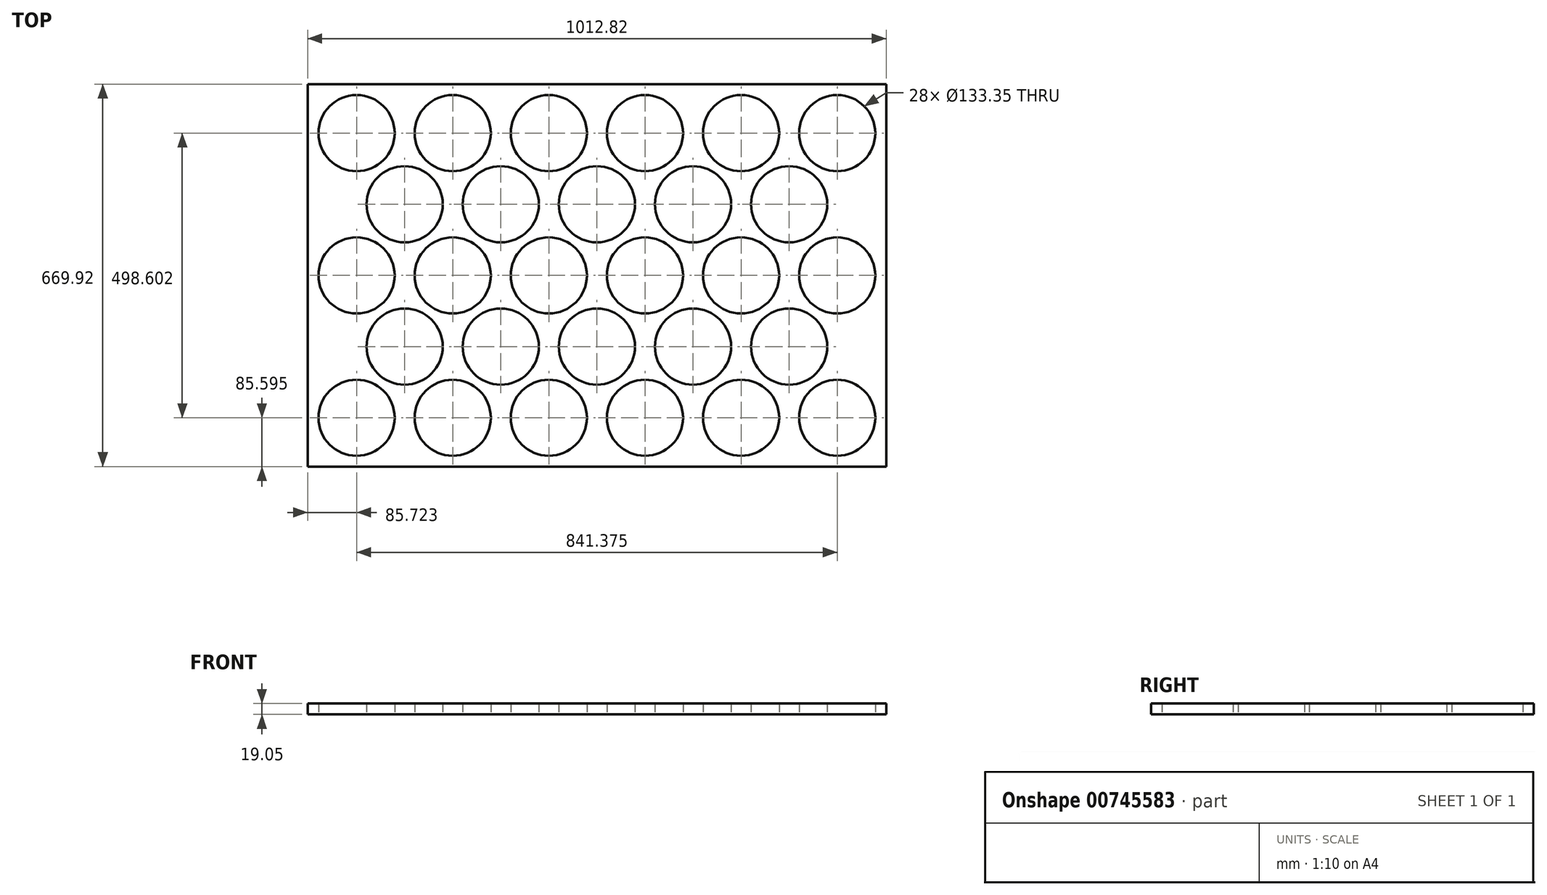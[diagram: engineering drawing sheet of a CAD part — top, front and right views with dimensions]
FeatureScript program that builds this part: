
annotation { "Feature Type Name" : "Feature", "Feature Type Description" : "" }
export const myFeature = defineFeature(function(context is Context, id is Id, definition is map)
    precondition{}
    {
        {
            var Q0;
            Q0=qCreatedBy(makeId("Top.planeOp"),FACE);
            var sketch = newSketch(context, id + "F0", { "sketchPlane" : qUnion([Q0])});
            skLineSegment(sketch, "E0.bottom", {"start": v(-506.41, 334.96) * mm, "end": v(506.41, 334.96) * mm});
            skLineSegment(sketch, "E0.top", {"start": v(-506.41, -334.96) * mm, "end": v(506.41, -334.96) * mm});
            skLineSegment(sketch, "E0.left", {"start": v(-506.41, 334.96) * mm, "end": v(-506.41, -334.96) * mm});
            skLineSegment(sketch, "E0.right", {"start": v(506.41, 334.96) * mm, "end": v(506.41, -334.96) * mm});
            skPoint(sketch, "E0.middle", {"position": v(0, 0) * mm});
            skCircle(sketch, "E1", {"center": v(-420.69, 249.24) * mm, "radius": 66.68 * mm});
            skLineSegment(sketch, "E2", {"start": v(-506.41, -334.96) * mm, "end": v(-506.41, -249.24) * mm, "construction": true});
            skLineSegment(sketch, "E3", {"start": v(-506.41, -249.24) * mm, "end": v(506.41, -249.24) * mm, "construction": true});
            skLineSegment(sketch, "E4", {"start": v(506.41, 334.96) * mm, "end": v(420.69, 334.96) * mm, "construction": true});
            skLineSegment(sketch, "E5", {"start": v(420.69, 334.96) * mm, "end": v(420.69, -249.24) * mm, "construction": true});
            skCircle(sketch, "E6.0.1.0", {"center": v(-420.69, -0.06) * mm, "radius": 66.68 * mm});
            skCircle(sketch, "E6.0.2.0", {"center": v(-420.69, -249.36) * mm, "radius": 66.68 * mm});
            skCircle(sketch, "E6.1.0.0", {"center": v(-252.41, 249.24) * mm, "radius": 66.68 * mm});
            skCircle(sketch, "E6.1.1.0", {"center": v(-252.41, -0.06) * mm, "radius": 66.68 * mm});
            skCircle(sketch, "E6.1.2.0", {"center": v(-252.41, -249.36) * mm, "radius": 66.68 * mm});
            skCircle(sketch, "E6.2.0.0", {"center": v(-84.14, 249.24) * mm, "radius": 66.68 * mm});
            skCircle(sketch, "E6.2.1.0", {"center": v(-84.14, -0.06) * mm, "radius": 66.68 * mm});
            skCircle(sketch, "E6.2.2.0", {"center": v(-84.14, -249.36) * mm, "radius": 66.68 * mm});
            skCircle(sketch, "E6.3.0.0", {"center": v(84.14, 249.24) * mm, "radius": 66.68 * mm});
            skCircle(sketch, "E6.3.1.0", {"center": v(84.14, -0.06) * mm, "radius": 66.68 * mm});
            skCircle(sketch, "E6.3.2.0", {"center": v(84.14, -249.36) * mm, "radius": 66.68 * mm});
            skCircle(sketch, "E6.4.0.0", {"center": v(252.41, 249.24) * mm, "radius": 66.68 * mm});
            skCircle(sketch, "E6.4.1.0", {"center": v(252.41, -0.06) * mm, "radius": 66.68 * mm});
            skCircle(sketch, "E6.4.2.0", {"center": v(252.41, -249.36) * mm, "radius": 66.68 * mm});
            skCircle(sketch, "E6.5.0.0", {"center": v(420.69, 249.24) * mm, "radius": 66.68 * mm});
            skCircle(sketch, "E6.5.1.0", {"center": v(420.69, -0.06) * mm, "radius": 66.68 * mm});
            skCircle(sketch, "E6.5.2.0", {"center": v(420.69, -249.36) * mm, "radius": 66.68 * mm});
            skLineSegment(sketch, "E6.direction1", {"start": v(-420.69, 249.24) * mm, "end": v(-252.41, 249.24) * mm, "construction": true});
            skLineSegment(sketch, "E6.direction2", {"start": v(-420.69, 249.24) * mm, "end": v(-420.69, -0.06) * mm, "construction": true});
            skLineSegment(sketch, "E7", {"start": v(-336.55, 249.24) * mm, "end": v(-336.55, 124.59) * mm, "construction": true});
            skCircle(sketch, "E8", {"center": v(-336.55, 124.59) * mm, "radius": 66.68 * mm});
            skCircle(sketch, "E9.0.1.0", {"center": v(-336.55, -124.71) * mm, "radius": 66.68 * mm});
            skCircle(sketch, "E9.1.0.0", {"center": v(-168.28, 124.59) * mm, "radius": 66.68 * mm});
            skCircle(sketch, "E9.1.1.0", {"center": v(-168.28, -124.71) * mm, "radius": 66.68 * mm});
            skCircle(sketch, "E9.2.0.0", {"center": v(0, 124.59) * mm, "radius": 66.68 * mm});
            skCircle(sketch, "E9.2.1.0", {"center": v(0, -124.71) * mm, "radius": 66.68 * mm});
            skCircle(sketch, "E9.3.0.0", {"center": v(168.28, 124.59) * mm, "radius": 66.68 * mm});
            skCircle(sketch, "E9.3.1.0", {"center": v(168.28, -124.71) * mm, "radius": 66.68 * mm});
            skCircle(sketch, "E9.4.0.0", {"center": v(336.55, 124.59) * mm, "radius": 66.68 * mm});
            skCircle(sketch, "E9.4.1.0", {"center": v(336.55, -124.71) * mm, "radius": 66.68 * mm});
            skLineSegment(sketch, "E9.direction1", {"start": v(-336.55, 124.59) * mm, "end": v(-168.28, 124.59) * mm, "construction": true});
            skLineSegment(sketch, "E9.direction2", {"start": v(-336.55, 124.59) * mm, "end": v(-336.55, -124.71) * mm, "construction": true});
            skSolve(sketch);
        }
        {
            var Q0;
            Q0 = qSketchRegion(id + "F0", true);
            extrude(context, id + "F1", {"entities" : qUnion([Q0]), "endBound" : BoundingType.SYMMETRIC, "depth" : 12.7 * mm, "offsetDistance" : 25.4 * mm});
        }
        {
            var Q0;
            Q0 = qSketchRegion(id + "F0", true);
            extrude(context, id + "F2", {"entities" : qUnion([Q0]), "operationType" : NewBodyOperationType.ADD, "depth" : 12.7 * mm, "offsetDistance" : 25.4 * mm});
        }
    });
